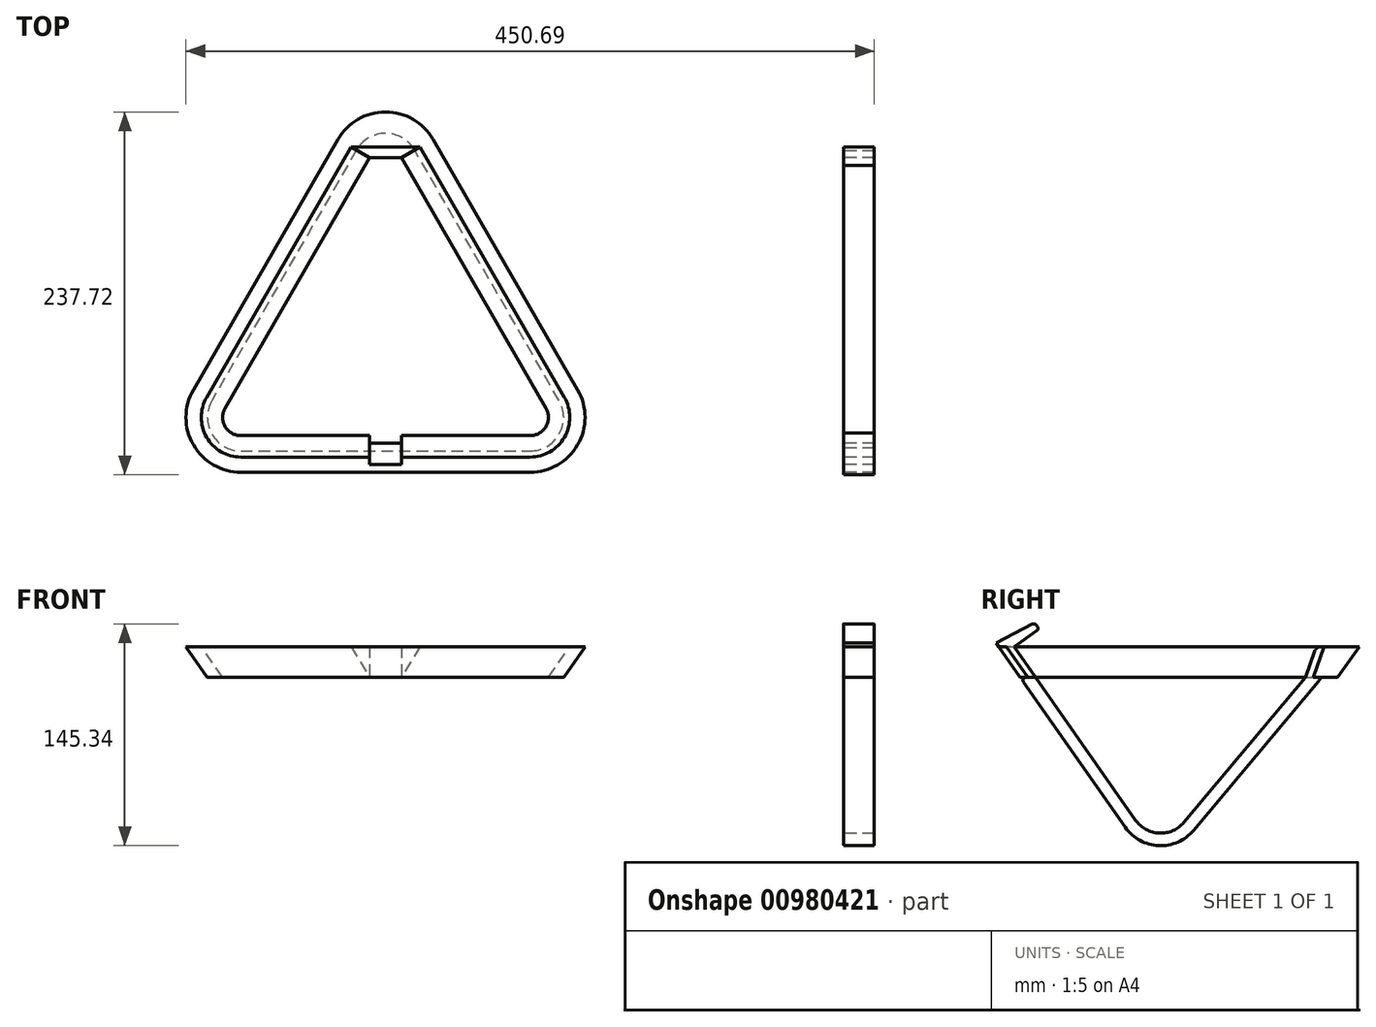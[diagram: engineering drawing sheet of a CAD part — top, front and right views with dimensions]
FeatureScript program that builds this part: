
annotation { "Feature Type Name" : "Feature", "Feature Type Description" : "" }
export const myFeature = defineFeature(function(context is Context, id is Id, definition is map)
    precondition{}
    {
        {
            var Q0;
            Q0=qCreatedBy(makeId("Top.planeOp"),FACE);
            var sketch = newSketch(context, id + "F0", { "sketchPlane" : qUnion([Q0])});
            skLineSegment(sketch, "E0", {"start": v(-94.69, 0) * mm, "end": v(94.69, 0) * mm});
            skLineSegment(sketch, "E1", {"start": v(105.08, 18) * mm, "end": v(10.4, 182) * mm});
            skLineSegment(sketch, "E2", {"start": v(-10.4, 182) * mm, "end": v(-105.08, 18) * mm});
            skLineSegment(sketch, "E3", {"start": v(0, 200) * mm, "end": v(0, 0) * mm, "construction": true});
            skPoint(sketch, "E4.visualSharp", {"position": v(0, 200) * mm});
            skArc(sketch, "E4.filletArc", {"start": v(10.4, 182) * mm, "mid": v(0, 188) * mm, "end": v(-10.4, 182) * mm});
            skPoint(sketch, "E5.visualSharp", {"position": v(115.47, 0) * mm});
            skArc(sketch, "E5.filletArc", {"start": v(94.69, 0) * mm, "mid": v(105.08, 6) * mm, "end": v(105.08, 18) * mm});
            skPoint(sketch, "E6.visualSharp", {"position": v(-115.47, 0) * mm});
            skArc(sketch, "E6.filletArc", {"start": v(-105.08, 18) * mm, "mid": v(-105.08, 6) * mm, "end": v(-94.69, 0) * mm});
            skArc(sketch, "E7.0", {"start": v(94.69, -10) * mm, "mid": v(113.74, 1) * mm, "end": v(113.74, 23) * mm});
            skArc(sketch, "E7.1", {"start": v(19.05, 187) * mm, "mid": v(0, 198) * mm, "end": v(-19.05, 187) * mm});
            skLineSegment(sketch, "E7.2", {"start": v(-19.05, 187) * mm, "end": v(-113.74, 23) * mm});
            skLineSegment(sketch, "E7.3", {"start": v(113.74, 23) * mm, "end": v(19.05, 187) * mm});
            skArc(sketch, "E7.4", {"start": v(-113.74, 23) * mm, "mid": v(-113.74, 1) * mm, "end": v(-94.69, -10) * mm});
            skLineSegment(sketch, "E7.5", {"start": v(-94.69, -10) * mm, "end": v(94.69, -10) * mm});
            skLineSegment(sketch, "E8", {"start": v(-10.4, 182) * mm, "end": v(10.4, 182) * mm});
            skSolve(sketch);
        }
        {
            var Q0;
            Q0=qCreatedBy(makeId("Right.planeOp"),FACE);
            var sketch = newSketch(context, id + "F1", { "sketchPlane" : qUnion([Q0])});
            skPoint(sketch, "E9.0", {"position": v(0, 0) * mm});
            skPoint(sketch, "E10.0", {"position": v(-10, 0) * mm});
            skLineSegment(sketch, "E11", {"start": v(0, 0) * mm, "end": v(-10, 0) * mm});
            skLineSegment(sketch, "E12", {"start": v(-10, 0) * mm, "end": v(-24, 20) * mm});
            skLineSegment(sketch, "E13", {"start": v(-24, 20) * mm, "end": v(-14, 20) * mm});
            skLineSegment(sketch, "E14", {"start": v(-14, 20) * mm, "end": v(0, 0) * mm});
            skSolve(sketch);
        }
        {
            var Q0;
            Q0=makeQuery(id+"F1.imprint","IMPRINT",FACE,{"disambiguationData":[TD([[makeQuery(id+"F1.imprint","IMPRINT",EDGE,{"derivedFrom":sQuery(id+"F1.wireOp",EDGE,"E11")}),-1.0]])]});
            var Q1;
            Q1=sQuery(id+"F0.wireOp",EDGE,"E0");
            var Q2;
            Q2=sQuery(id+"F0.wireOp",EDGE,"E6.filletArc");
            var Q3;
            Q3=sQuery(id+"F0.wireOp",EDGE,"E2");
            var Q4;
            Q4=sQuery(id+"F0.wireOp",EDGE,"E4.filletArc");
            var Q5;
            Q5=sQuery(id+"F0.wireOp",EDGE,"E1");
            var Q6;
            Q6=sQuery(id+"F0.wireOp",EDGE,"E5.filletArc");
            sweep(context, id + "F2", {"profiles" : qUnion([Q0]), "path" : qUnion([Q1, Q2, Q3, Q4, Q5, Q6])});
        }
        {
            var Q0;
            Q0=makeQuery(id+"F2.opSweep","SWEPT_FACE",FACE,{"disambiguationData":[OSD([sQuery(id+"F0.wireOp",EDGE,"E0"),sQuery(id+"F1.wireOp",EDGE,"E13")])]});
            var sketch = newSketch(context, id + "F3", { "sketchPlane" : qUnion([Q0])});
            skArc(sketch, "E15.0", {"start": v(22.52, 189) * mm, "mid": v(0, 202) * mm, "end": v(-22.52, 189) * mm});
            skLineSegment(sketch, "E16", {"start": v(-22.52, 189) * mm, "end": v(22.52, 189) * mm});
            skSolve(sketch);
        }
        {
            var Q1;
            Q1=makeQuery(id+"F0.imprint","IMPRINT",FACE,{"disambiguationData":[TD([[makeQuery(id+"F0.imprint","IMPRINT",EDGE,{"derivedFrom":sQuery(id+"F0.wireOp",EDGE,"E4.filletArc")}),1.0]])]});
            var Q2;
            Q2=makeQuery(id+"F3.imprint","IMPRINT",FACE,{"disambiguationData":[TD([[makeQuery(id+"F3.imprint","IMPRINT",EDGE,{"derivedFrom":sQuery(id+"F3.wireOp",EDGE,"E15.0")}),1.0]])]});
            loft(context, id + "F4", {"operationType" : NewBodyOperationType.ADD, "sheetProfilesArray" : [{ "sheetProfileEntities" : qUnion([Q1]) }, { "sheetProfileEntities" : qUnion([Q2]) }]});
        }
        {
            var Q0;
            Q0=qCreatedBy(makeId("Right.planeOp"),FACE);
            cPlane(context, id + "F5", {"entities" : qUnion([Q0]), "cplaneType" : CPlaneType.OFFSET, "offset" : 300 * mm, "width" : 150 * mm, "height" : 150 * mm});
        }
        {
            var Q0;
            Q0=qCreatedBy(id+"F5.planeOp",FACE);
            var sketch = newSketch(context, id + "F6", { "sketchPlane" : qUnion([Q0])});
            skLineSegment(sketch, "E17.0", {"start": v(182, 0) * mm, "end": v(189, 20) * mm});
            skLineSegment(sketch, "E18.0", {"start": v(-24, 20) * mm, "end": v(-10, 0) * mm, "construction": true});
            skLineSegment(sketch, "E19.0", {"start": v(0, 0) * mm, "end": v(-14, 20) * mm, "construction": true});
            skLineSegment(sketch, "E20.0", {"start": v(187, 0) * mm, "end": v(198, 0) * mm, "construction": true});
            skLineSegment(sketch, "E21", {"start": v(189, 20) * mm, "end": v(186.84, 20) * mm});
            skLineSegment(sketch, "E22", {"start": v(183.06, 17.32) * mm, "end": v(177, 0) * mm});
            skLineSegment(sketch, "E23", {"start": v(177, 0) * mm, "end": v(97.27, -95.02) * mm});
            skLineSegment(sketch, "E24", {"start": v(65.56, -93.64) * mm, "end": v(0, 0) * mm});
            skLineSegment(sketch, "E25", {"start": v(182, 0) * mm, "end": v(187.7, 0) * mm});
            skLineSegment(sketch, "E26", {"start": v(187.7, 0) * mm, "end": v(185.54, -2.57) * mm, "construction": true});
            skLineSegment(sketch, "E27", {"start": v(58.85, -98.33) * mm, "end": v(-7.8, -3.15) * mm});
            skPoint(sketch, "E28.visualSharp", {"position": v(80.51, -114.99) * mm});
            skArc(sketch, "E28.filletArc", {"start": v(65.56, -93.64) * mm, "mid": v(81.08, -102.15) * mm, "end": v(97.27, -95.02) * mm});
            skPoint(sketch, "E29.visualSharp", {"position": v(79.93, -128.43) * mm});
            skArc(sketch, "E29.filletArc", {"start": v(58.85, -98.33) * mm, "mid": v(80.72, -110.33) * mm, "end": v(103.54, -100.29) * mm});
            skLineSegment(sketch, "E30", {"start": v(32.78, -46.82) * mm, "end": v(26.07, -51.52) * mm, "construction": true});
            skLineSegment(sketch, "E31", {"start": v(137.13, -47.51) * mm, "end": v(143.4, -52.78) * mm, "construction": true});
            skLineSegment(sketch, "E32", {"start": v(81.08, -102.15) * mm, "end": v(80.72, -110.33) * mm, "construction": true});
            skPoint(sketch, "E33.visualSharp", {"position": v(184, 20) * mm});
            skArc(sketch, "E33.filletArc", {"start": v(186.84, 20) * mm, "mid": v(184.53, 19.26) * mm, "end": v(183.06, 17.32) * mm});
            skArc(sketch, "E34", {"start": v(185.54, -2.57) * mm, "mid": v(186.23, -1.37) * mm, "end": v(186.47, 0) * mm});
            skLineSegment(sketch, "E35", {"start": v(185.54, -2.57) * mm, "end": v(103.54, -100.29) * mm});
            skLineSegment(sketch, "E36", {"start": v(0, 0) * mm, "end": v(-14, 20) * mm});
            skLineSegment(sketch, "E37", {"start": v(-14, 20) * mm, "end": v(0.74, 30.32) * mm});
            skLineSegment(sketch, "E38", {"start": v(1.23, 33.1) * mm, "end": v(0.52, 34.13) * mm});
            skLineSegment(sketch, "E39", {"start": v(-2.04, 34.76) * mm, "end": v(-25.72, 22.46) * mm});
            skLineSegment(sketch, "E40", {"start": v(-25.72, 22.46) * mm, "end": v(-24, 20) * mm});
            skLineSegment(sketch, "E41", {"start": v(-5, 0) * mm, "end": v(-19, 20) * mm});
            skLineSegment(sketch, "E42", {"start": v(-19, 20) * mm, "end": v(-24, 20) * mm});
            skLineSegment(sketch, "E43", {"start": v(-5, 0) * mm, "end": v(-6.16, 0) * mm});
            skLineSegment(sketch, "E44", {"start": v(0, 0) * mm, "end": v(-5, 0) * mm, "construction": true});
            skPoint(sketch, "E45.visualSharp", {"position": v(-10, 0) * mm});
            skArc(sketch, "E45.filletArc", {"start": v(-6.16, 0) * mm, "mid": v(-7.93, -1.08) * mm, "end": v(-7.8, -3.15) * mm});
            skPoint(sketch, "E46.visualSharp", {"position": v(2.38, 31.47) * mm});
            skArc(sketch, "E46.filletArc", {"start": v(0.74, 30.32) * mm, "mid": v(1.56, 31.62) * mm, "end": v(1.23, 33.1) * mm});
            skPoint(sketch, "E47.visualSharp", {"position": v(-0.49, 35.57) * mm});
            skArc(sketch, "E47.filletArc", {"start": v(0.52, 34.13) * mm, "mid": v(-0.65, 34.93) * mm, "end": v(-2.04, 34.76) * mm});
            skSolve(sketch);
        }
        {
            var Q0;
            Q0 = qSketchRegion(id + "F6", true);
            extrude(context, id + "F7", {"entities" : qUnion([Q0]), "depth" : 20 * mm, "offsetDistance" : 25 * mm});
        }
        {
            var Q0;
            Q0=qCreatedBy(makeId("Right.planeOp"),FACE);
            var sketch = newSketch(context, id + "F8", { "sketchPlane" : qUnion([Q0])});
            skLineSegment(sketch, "E48.0", {"start": v(-5, 0) * mm, "end": v(-19, 20) * mm});
            skLineSegment(sketch, "E49", {"start": v(-19, 20) * mm, "end": v(-9, 20) * mm});
            skLineSegment(sketch, "E50", {"start": v(-9, 20) * mm, "end": v(5, 0) * mm});
            skLineSegment(sketch, "E51", {"start": v(5, 0) * mm, "end": v(-5, 0) * mm});
            skSolve(sketch);
        }
        {
            var Q0;
            Q0 = qSketchRegion(id + "F8", true);
            extrude(context, id + "F9", {"entities" : qUnion([Q0]), "operationType" : NewBodyOperationType.REMOVE, "endBound" : BoundingType.SYMMETRIC, "oppositeDirection" : true, "depth" : 21 * mm, "offsetDistance" : 25 * mm});
        }
    });
